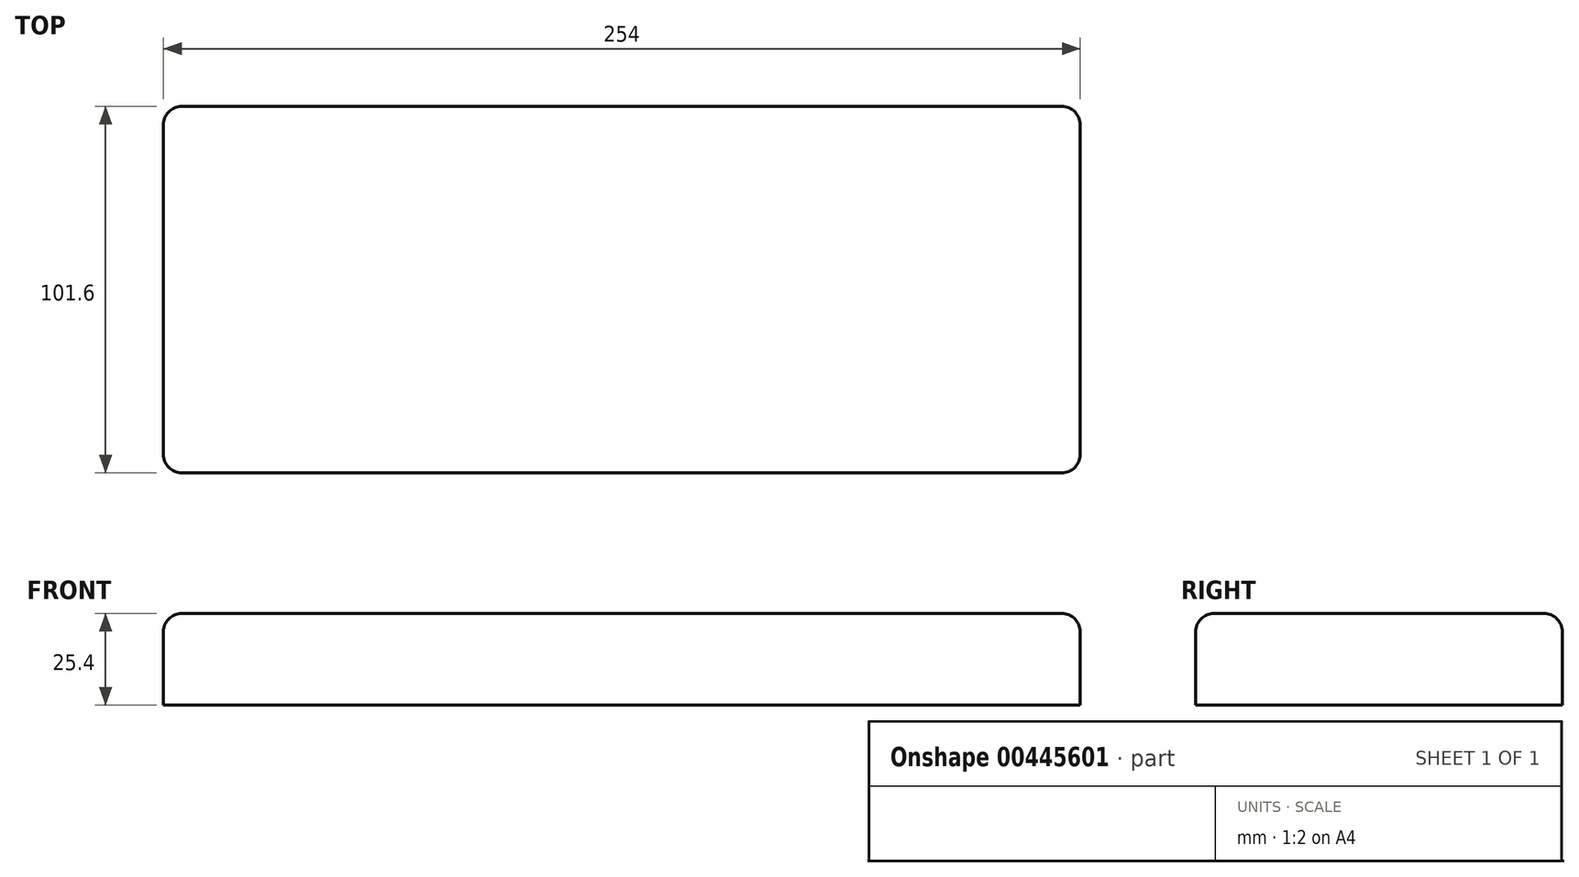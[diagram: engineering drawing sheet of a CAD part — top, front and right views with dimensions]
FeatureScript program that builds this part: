
annotation { "Feature Type Name" : "Feature", "Feature Type Description" : "" }
export const myFeature = defineFeature(function(context is Context, id is Id, definition is map)
    precondition{}
    {
        {
            var Q0;
            Q0=qCreatedBy(makeId("Top.planeOp"),FACE);
            var sketch = newSketch(context, id + "F0", { "sketchPlane" : qUnion([Q0])});
            skLineSegment(sketch, "E0.bottom", {"start": v(-127, -50.8) * mm, "end": v(127, -50.8) * mm});
            skLineSegment(sketch, "E0.top", {"start": v(-127, 50.8) * mm, "end": v(127, 50.8) * mm});
            skLineSegment(sketch, "E0.left", {"start": v(-127, -50.8) * mm, "end": v(-127, 50.8) * mm});
            skLineSegment(sketch, "E0.right", {"start": v(127, -50.8) * mm, "end": v(127, 50.8) * mm});
            skPoint(sketch, "E0.middle", {"position": v(0, 0) * mm});
            skSolve(sketch);
        }
        {
            var Q0;
            Q0 = qSketchRegion(id + "F0", true);
            extrude(context, id + "F1", {"entities" : qUnion([Q0]), "depth" : 25.4 * mm});
        }
        {
            var Q0;
            Q0=makeQuery(id+"F1.opExtrude","CAP_EDGE",EDGE,{"disambiguationData":[OSD([sQuery(id+"F0.wireOp",EDGE,"E0.bottom")])],"isStart":false});
            fillet(context, id + "F2", {"entities" : qUnion([Q0]), "radius" : 5.08 * mm, "tangentPropagation" : true, "allowEdgeOverflow" : false});
        }
        {
            var Q0;
            Q0=makeQuery(id+"F1.opExtrude","CAP_EDGE",EDGE,{"disambiguationData":[OSD([sQuery(id+"F0.wireOp",EDGE,"E0.right")])],"isStart":false});
            var Q1;
            Q1=makeQuery(id+"F1.opExtrude","CAP_EDGE",EDGE,{"disambiguationData":[OSD([sQuery(id+"F0.wireOp",EDGE,"E0.top")])],"isStart":false});
            var Q2;
            Q2=makeQuery(id+"F1.opExtrude","CAP_EDGE",EDGE,{"disambiguationData":[OSD([sQuery(id+"F0.wireOp",EDGE,"E0.left")])],"isStart":false});
            fillet(context, id + "F3", {"entities" : qUnion([Q0, Q1, Q2]), "radius" : 5.08 * mm, "tangentPropagation" : true, "allowEdgeOverflow" : false});
        }
        {
            var Q0;
            Q0=makeQuery(id+"F1.opExtrude","SWEPT_EDGE",EDGE,{"disambiguationData":[OSD([sQuery(id+"F0.wireOp",EDGE,"E0.top"),sQuery(id+"F0.wireOp",EDGE,"E0.right")])]});
            fillet(context, id + "F4", {"entities" : qUnion([Q0]), "radius" : 5.08 * mm, "tangentPropagation" : true, "allowEdgeOverflow" : false});
        }
        {
            var Q0;
            Q0=makeQuery(id+"F1.opExtrude","SWEPT_EDGE",EDGE,{"disambiguationData":[OSD([sQuery(id+"F0.wireOp",EDGE,"E0.top"),sQuery(id+"F0.wireOp",EDGE,"E0.left")])]});
            fillet(context, id + "F5", {"entities" : qUnion([Q0]), "radius" : 5.08 * mm, "tangentPropagation" : true, "allowEdgeOverflow" : false});
        }
    });
